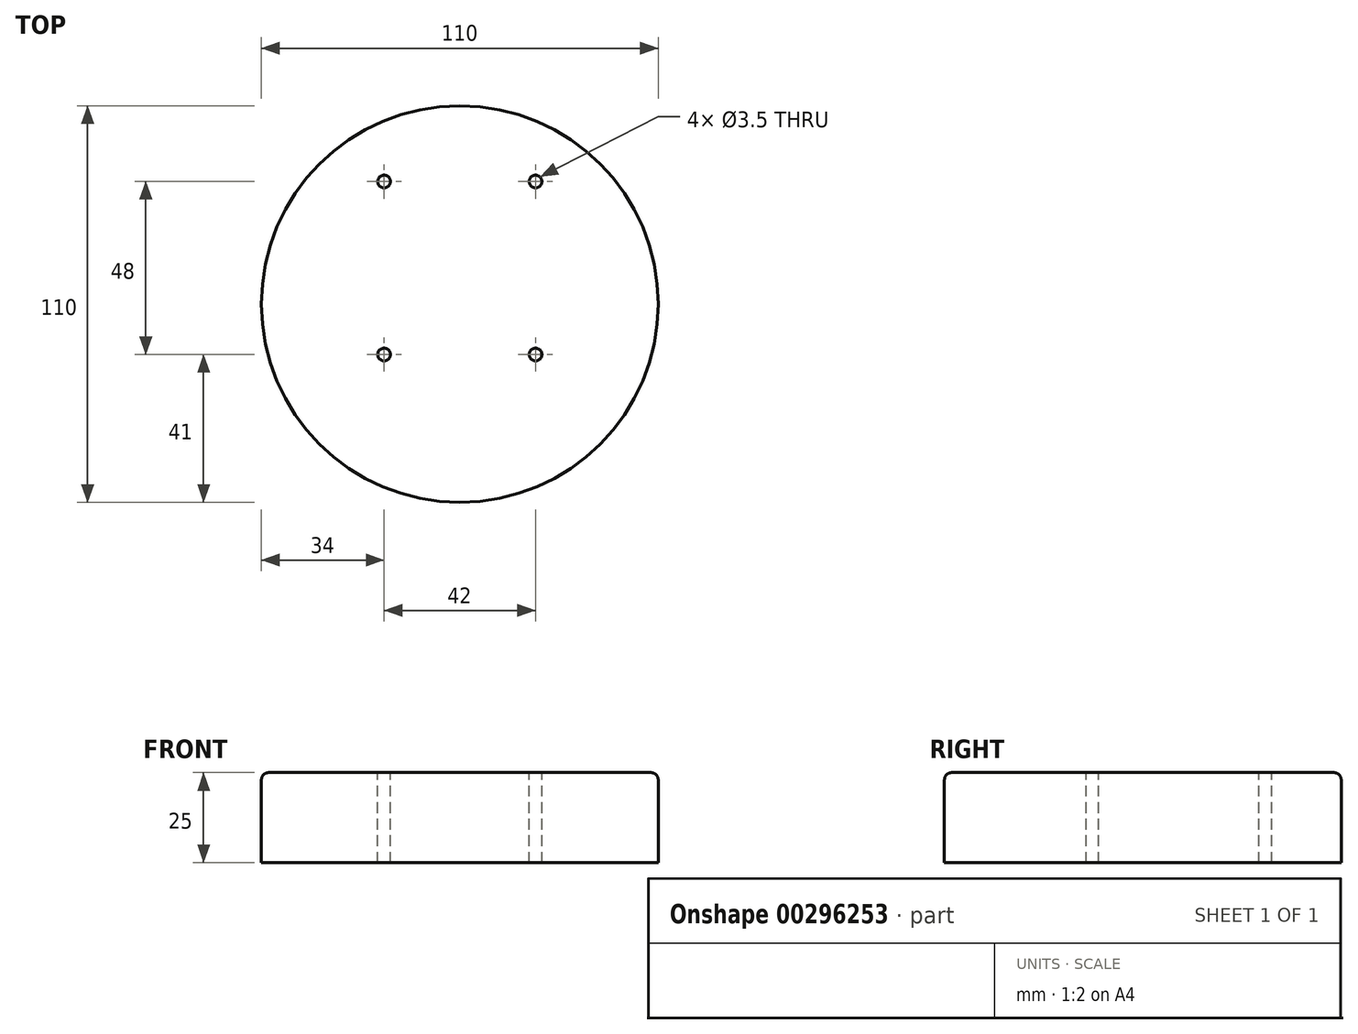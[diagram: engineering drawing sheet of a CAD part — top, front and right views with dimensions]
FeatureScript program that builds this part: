
annotation { "Feature Type Name" : "Feature", "Feature Type Description" : "" }
export const myFeature = defineFeature(function(context is Context, id is Id, definition is map)
    precondition{}
    {
        {
            var Q0;
            Q0=qCreatedBy(makeId("Top.planeOp"),FACE);
            var sketch = newSketch(context, id + "F0", { "sketchPlane" : qUnion([Q0])});
            skCircle(sketch, "E0", {"center": v(0, 0) * mm, "radius": 55 * mm});
            skSolve(sketch);
        }
        {
            var Q0;
            Q0=makeQuery(id+"F0.imprint","IMPRINT",FACE,{"disambiguationData":[TD([[makeQuery(id+"F0.imprint","IMPRINT",EDGE,{"derivedFrom":sQuery(id+"F0.wireOp",EDGE,"E0")}),1.0]])]});
            extrude(context, id + "F1", {"entities" : qUnion([Q0]), "depth" : 25 * mm});
        }
        {
            var Q0;
            Q0=makeQuery(id+"F1.opExtrude","CAP_EDGE",EDGE,{"disambiguationData":[OSD([sQuery(id+"F0.wireOp",EDGE,"E0")])],"isStart":false});
            fillet(context, id + "F2", {"entities" : qUnion([Q0]), "radius" : 2 * mm, "tangentPropagation" : true, "allowEdgeOverflow" : false});
        }
        {
            var Q0;
            Q0=makeQuery(id+"F1.opExtrude","CAP_FACE",FACE,{"disambiguationData":[OSD([sQuery(id+"F0.wireOp",EDGE,"E0")])],"isStart":false});
            var sketch = newSketch(context, id + "F3", { "sketchPlane" : qUnion([Q0])});
            skPoint(sketch, "E1", {"position": v(-21, -14) * mm});
            skPoint(sketch, "E2", {"position": v(21, -14) * mm});
            skPoint(sketch, "E3", {"position": v(21, 34) * mm});
            skPoint(sketch, "E4", {"position": v(-21, 34) * mm});
            skLineSegment(sketch, "E5", {"start": v(-21, -14) * mm, "end": v(21, -14) * mm, "construction": true});
            skCircle(sketch, "E6", {"center": v(-21, 34) * mm, "radius": 1.75 * mm});
            skCircle(sketch, "E7", {"center": v(21, 34) * mm, "radius": 1.75 * mm});
            skCircle(sketch, "E8", {"center": v(-21, -14) * mm, "radius": 1.75 * mm});
            skCircle(sketch, "E9", {"center": v(21, -14) * mm, "radius": 1.75 * mm});
            skSolve(sketch);
        }
        {
            var Q0;
            Q0=makeQuery(id+"F3.imprint","IMPRINT",FACE,{"disambiguationData":[TD([[makeQuery(id+"F3.imprint","IMPRINT",EDGE,{"derivedFrom":sQuery(id+"F3.wireOp",EDGE,"E6")}),1.0]])]});
            var Q1;
            Q1=makeQuery(id+"F3.imprint","IMPRINT",FACE,{"disambiguationData":[TD([[makeQuery(id+"F3.imprint","IMPRINT",EDGE,{"derivedFrom":sQuery(id+"F3.wireOp",EDGE,"E7")}),1.0]])]});
            var Q2;
            Q2=makeQuery(id+"F3.imprint","IMPRINT",FACE,{"disambiguationData":[TD([[makeQuery(id+"F3.imprint","IMPRINT",EDGE,{"derivedFrom":sQuery(id+"F3.wireOp",EDGE,"E9")}),1.0]])]});
            var Q3;
            Q3=makeQuery(id+"F3.imprint","IMPRINT",FACE,{"disambiguationData":[TD([[makeQuery(id+"F3.imprint","IMPRINT",EDGE,{"derivedFrom":sQuery(id+"F3.wireOp",EDGE,"E8")}),1.0]])]});
            extrude(context, id + "F4", {"entities" : qUnion([Q0, Q1, Q2, Q3]), "operationType" : NewBodyOperationType.REMOVE, "endBound" : BoundingType.UP_TO_NEXT, "oppositeDirection" : true, "depth" : 25 * mm});
        }
    });
